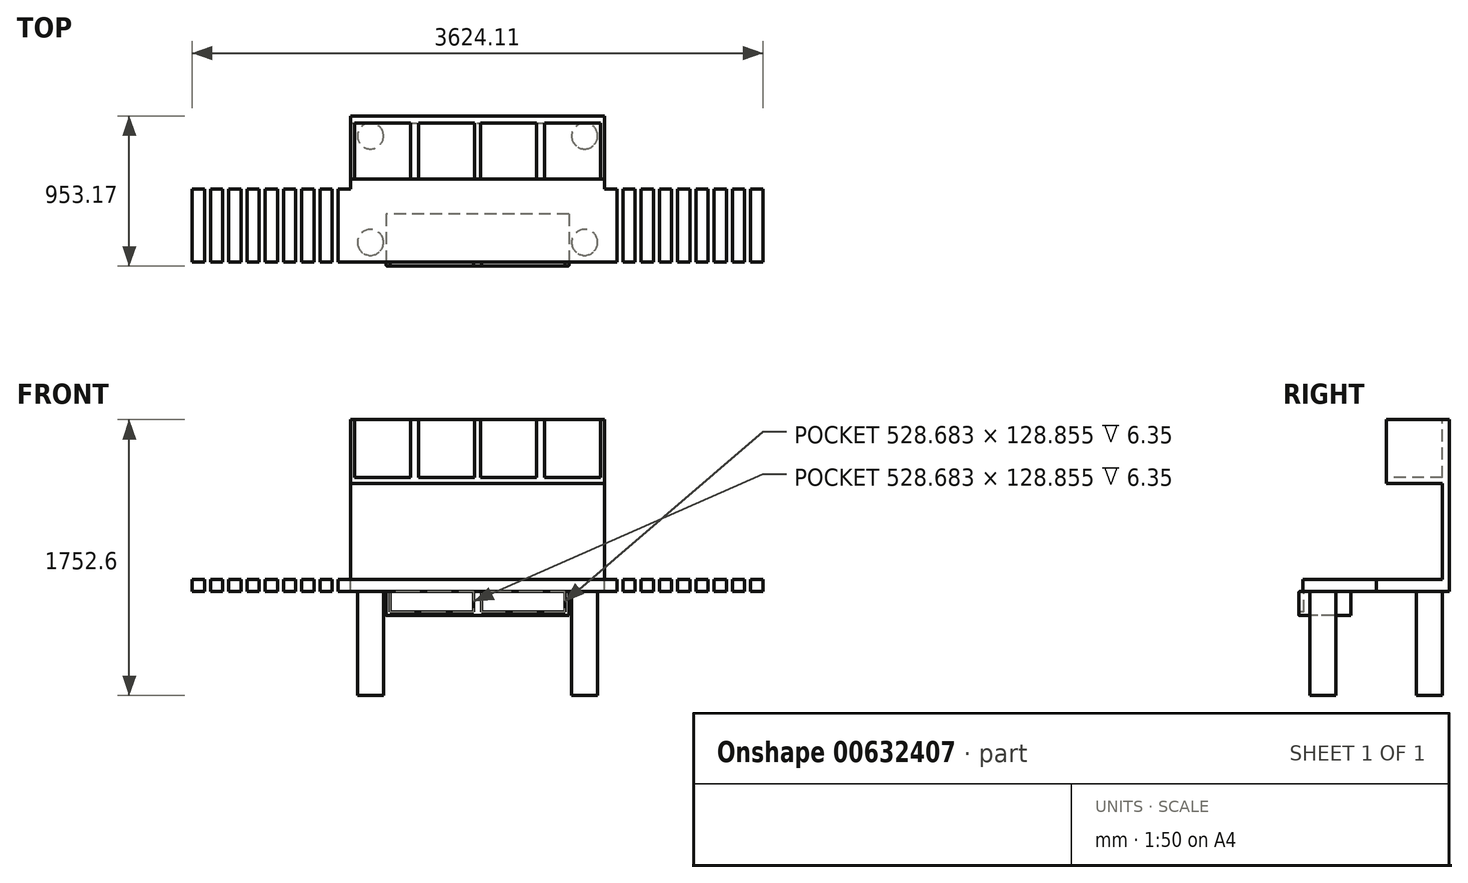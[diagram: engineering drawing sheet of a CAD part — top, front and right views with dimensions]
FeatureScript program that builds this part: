
annotation { "Feature Type Name" : "Feature", "Feature Type Description" : "" }
export const myFeature = defineFeature(function(context is Context, id is Id, definition is map)
    precondition{}
    {
        {
            var Q0;
            Q0=qCreatedBy(makeId("Top.planeOp"),FACE);
            var sketch = newSketch(context, id + "F0", { "sketchPlane" : qUnion([Q0])});
            skLineSegment(sketch, "E0.bottom", {"start": v(0, 0) * mm, "end": v(1613.94, 0) * mm});
            skLineSegment(sketch, "E0.top", {"start": v(0, 927.77) * mm, "end": v(1613.94, 927.77) * mm});
            skLineSegment(sketch, "E0.left", {"start": v(0, 0) * mm, "end": v(0, 927.77) * mm});
            skLineSegment(sketch, "E0.right", {"start": v(1613.94, 0) * mm, "end": v(1613.94, 927.77) * mm});
            skPoint(sketch, "E1", {"position": v(806.97, 0) * mm});
            skPoint(sketch, "E2", {"position": v(1613.94, 463.89) * mm});
            skLineSegment(sketch, "E3.bottom", {"start": v(1613.94, 463.89) * mm, "end": v(1691.25, 463.89) * mm});
            skLineSegment(sketch, "E3.top", {"start": v(1613.94, 0) * mm, "end": v(1691.25, 0) * mm});
            skLineSegment(sketch, "E3.left", {"start": v(1613.94, 463.89) * mm, "end": v(1613.94, 0) * mm});
            skLineSegment(sketch, "E3.right", {"start": v(1691.25, 463.89) * mm, "end": v(1691.25, 0) * mm});
            skPoint(sketch, "E4", {"position": v(1729.9, 463.89) * mm});
            skPoint(sketch, "E5", {"position": v(1729.9, 0) * mm});
            skLineSegment(sketch, "E6.bottom", {"start": v(1729.9, 463.89) * mm, "end": v(1807.22, 463.89) * mm});
            skLineSegment(sketch, "E6.top", {"start": v(1729.9, 0) * mm, "end": v(1807.22, 0) * mm});
            skLineSegment(sketch, "E6.left", {"start": v(1729.9, 463.89) * mm, "end": v(1729.9, 0) * mm});
            skLineSegment(sketch, "E6.right", {"start": v(1807.22, 463.89) * mm, "end": v(1807.22, 0) * mm});
            skPoint(sketch, "E7", {"position": v(1845.88, 463.89) * mm});
            skPoint(sketch, "E8", {"position": v(1845.88, 0) * mm});
            skLineSegment(sketch, "E9.bottom", {"start": v(1845.88, 463.89) * mm, "end": v(1923.2, 463.89) * mm});
            skLineSegment(sketch, "E9.top", {"start": v(1845.88, 0) * mm, "end": v(1923.2, 0) * mm});
            skLineSegment(sketch, "E9.left", {"start": v(1845.88, 463.89) * mm, "end": v(1845.88, 0) * mm});
            skLineSegment(sketch, "E9.right", {"start": v(1923.2, 463.89) * mm, "end": v(1923.2, 0) * mm});
            skPoint(sketch, "E10", {"position": v(1961.85, 463.89) * mm});
            skPoint(sketch, "E11", {"position": v(1961.85, 0) * mm});
            skLineSegment(sketch, "E12.bottom", {"start": v(1961.85, 463.89) * mm, "end": v(2039.17, 463.89) * mm});
            skLineSegment(sketch, "E12.top", {"start": v(1961.85, 0) * mm, "end": v(2039.17, 0) * mm});
            skLineSegment(sketch, "E12.left", {"start": v(1961.85, 463.89) * mm, "end": v(1961.85, 0) * mm});
            skLineSegment(sketch, "E12.right", {"start": v(2039.17, 463.89) * mm, "end": v(2039.17, 0) * mm});
            skPoint(sketch, "E13", {"position": v(2077.82, 463.89) * mm});
            skPoint(sketch, "E14", {"position": v(2077.82, 0) * mm});
            skLineSegment(sketch, "E15.bottom", {"start": v(2077.82, 463.89) * mm, "end": v(2155.14, 463.89) * mm});
            skLineSegment(sketch, "E15.top", {"start": v(2077.82, 0) * mm, "end": v(2155.14, 0) * mm});
            skLineSegment(sketch, "E15.left", {"start": v(2077.82, 463.89) * mm, "end": v(2077.82, 0) * mm});
            skLineSegment(sketch, "E15.right", {"start": v(2155.14, 463.89) * mm, "end": v(2155.14, 0) * mm});
            skPoint(sketch, "E16", {"position": v(2193.8, 463.89) * mm});
            skPoint(sketch, "E17", {"position": v(2193.8, 0) * mm});
            skLineSegment(sketch, "E18.bottom", {"start": v(2193.8, 463.89) * mm, "end": v(2271.1, 463.89) * mm});
            skLineSegment(sketch, "E18.top", {"start": v(2193.8, 0) * mm, "end": v(2271.1, 0) * mm});
            skLineSegment(sketch, "E18.left", {"start": v(2193.8, 463.89) * mm, "end": v(2193.8, 0) * mm});
            skLineSegment(sketch, "E18.right", {"start": v(2271.1, 463.89) * mm, "end": v(2271.1, 0) * mm});
            skPoint(sketch, "E19", {"position": v(2309.77, 463.89) * mm});
            skPoint(sketch, "E20", {"position": v(2309.77, 0) * mm});
            skLineSegment(sketch, "E21.bottom", {"start": v(2309.77, 463.89) * mm, "end": v(2387.08, 463.89) * mm});
            skLineSegment(sketch, "E21.top", {"start": v(2309.77, 0) * mm, "end": v(2387.08, 0) * mm});
            skLineSegment(sketch, "E21.left", {"start": v(2309.77, 463.89) * mm, "end": v(2309.77, 0) * mm});
            skLineSegment(sketch, "E21.right", {"start": v(2387.08, 463.89) * mm, "end": v(2387.08, 0) * mm});
            skPoint(sketch, "E22", {"position": v(2425.74, 463.89) * mm});
            skPoint(sketch, "E23", {"position": v(2425.74, 0) * mm});
            skLineSegment(sketch, "E24.bottom", {"start": v(2425.74, 463.89) * mm, "end": v(2503.05, 463.89) * mm});
            skLineSegment(sketch, "E24.top", {"start": v(2425.74, 0) * mm, "end": v(2503.05, 0) * mm});
            skLineSegment(sketch, "E24.left", {"start": v(2425.74, 463.89) * mm, "end": v(2425.74, 0) * mm});
            skLineSegment(sketch, "E24.right", {"start": v(2503.05, 463.89) * mm, "end": v(2503.05, 0) * mm});
            skPoint(sketch, "E25", {"position": v(2541.7, 463.89) * mm});
            skPoint(sketch, "E26", {"position": v(2541.7, 0) * mm});
            skLineSegment(sketch, "E27.bottom", {"start": v(2541.7, 463.89) * mm, "end": v(2619.02, 463.89) * mm});
            skLineSegment(sketch, "E27.top", {"start": v(2541.7, 0) * mm, "end": v(2619.02, 0) * mm});
            skLineSegment(sketch, "E27.left", {"start": v(2541.7, 463.89) * mm, "end": v(2541.7, 0) * mm});
            skLineSegment(sketch, "E27.right", {"start": v(2619.02, 463.89) * mm, "end": v(2619.02, 0) * mm});
            skPoint(sketch, "E28", {"position": v(-1005.09, 463.89) * mm});
            skPoint(sketch, "E29", {"position": v(-1005.09, 0) * mm});
            skLineSegment(sketch, "E30.bottom", {"start": v(-1005.09, 463.89) * mm, "end": v(-927.77, 463.89) * mm});
            skLineSegment(sketch, "E30.top", {"start": v(-1005.09, 0) * mm, "end": v(-927.77, 0) * mm});
            skLineSegment(sketch, "E30.left", {"start": v(-1005.09, 463.89) * mm, "end": v(-1005.09, 0) * mm});
            skLineSegment(sketch, "E30.right", {"start": v(-927.77, 463.89) * mm, "end": v(-927.77, 0) * mm});
            skPoint(sketch, "E31", {"position": v(-889.11, 463.89) * mm});
            skPoint(sketch, "E32", {"position": v(-889.11, 0) * mm});
            skLineSegment(sketch, "E33.bottom", {"start": v(-889.11, 463.89) * mm, "end": v(-811.8, 463.89) * mm});
            skLineSegment(sketch, "E33.top", {"start": v(-889.11, 0) * mm, "end": v(-811.8, 0) * mm});
            skLineSegment(sketch, "E33.left", {"start": v(-889.11, 463.89) * mm, "end": v(-889.11, 0) * mm});
            skLineSegment(sketch, "E33.right", {"start": v(-811.8, 463.89) * mm, "end": v(-811.8, 0) * mm});
            skPoint(sketch, "E34", {"position": v(-773.14, 463.89) * mm});
            skPoint(sketch, "E35", {"position": v(-773.14, 0) * mm});
            skLineSegment(sketch, "E36.bottom", {"start": v(-773.14, 463.89) * mm, "end": v(-695.83, 463.89) * mm});
            skLineSegment(sketch, "E36.top", {"start": v(-773.14, 0) * mm, "end": v(-695.83, 0) * mm});
            skLineSegment(sketch, "E36.left", {"start": v(-773.14, 463.89) * mm, "end": v(-773.14, 0) * mm});
            skLineSegment(sketch, "E36.right", {"start": v(-695.83, 463.89) * mm, "end": v(-695.83, 0) * mm});
            skPoint(sketch, "E37", {"position": v(-657.17, 463.89) * mm});
            skPoint(sketch, "E38", {"position": v(-657.17, 0) * mm});
            skLineSegment(sketch, "E39.bottom", {"start": v(-657.17, 463.89) * mm, "end": v(-579.86, 463.89) * mm});
            skLineSegment(sketch, "E39.top", {"start": v(-657.17, 0) * mm, "end": v(-579.86, 0) * mm});
            skLineSegment(sketch, "E39.left", {"start": v(-657.17, 463.89) * mm, "end": v(-657.17, 0) * mm});
            skLineSegment(sketch, "E39.right", {"start": v(-579.86, 463.89) * mm, "end": v(-579.86, 0) * mm});
            skPoint(sketch, "E40", {"position": v(-541.2, 463.89) * mm});
            skPoint(sketch, "E41", {"position": v(-541.2, 0) * mm});
            skLineSegment(sketch, "E42.bottom", {"start": v(-541.2, 463.89) * mm, "end": v(-463.89, 463.89) * mm});
            skLineSegment(sketch, "E42.top", {"start": v(-541.2, 0) * mm, "end": v(-463.89, 0) * mm});
            skLineSegment(sketch, "E42.left", {"start": v(-541.2, 463.89) * mm, "end": v(-541.2, 0) * mm});
            skLineSegment(sketch, "E42.right", {"start": v(-463.89, 463.89) * mm, "end": v(-463.89, 0) * mm});
            skPoint(sketch, "E43", {"position": v(-425.23, 463.89) * mm});
            skPoint(sketch, "E44", {"position": v(-425.23, 0) * mm});
            skLineSegment(sketch, "E45.bottom", {"start": v(-425.23, 463.89) * mm, "end": v(-347.91, 463.89) * mm});
            skLineSegment(sketch, "E45.top", {"start": v(-425.23, 0) * mm, "end": v(-347.91, 0) * mm});
            skLineSegment(sketch, "E45.left", {"start": v(-425.23, 463.89) * mm, "end": v(-425.23, 0) * mm});
            skLineSegment(sketch, "E45.right", {"start": v(-347.91, 463.89) * mm, "end": v(-347.91, 0) * mm});
            skPoint(sketch, "E46", {"position": v(-309.26, 463.89) * mm});
            skPoint(sketch, "E47", {"position": v(-309.26, 0) * mm});
            skLineSegment(sketch, "E48.bottom", {"start": v(-309.26, 463.89) * mm, "end": v(-231.94, 463.89) * mm});
            skLineSegment(sketch, "E48.top", {"start": v(-309.26, 0) * mm, "end": v(-231.94, 0) * mm});
            skLineSegment(sketch, "E48.left", {"start": v(-309.26, 463.89) * mm, "end": v(-309.26, 0) * mm});
            skLineSegment(sketch, "E48.right", {"start": v(-231.94, 463.89) * mm, "end": v(-231.94, 0) * mm});
            skPoint(sketch, "E49", {"position": v(-193.29, 463.89) * mm});
            skPoint(sketch, "E50", {"position": v(-193.29, 0) * mm});
            skLineSegment(sketch, "E51.bottom", {"start": v(-193.29, 463.89) * mm, "end": v(-115.97, 463.89) * mm});
            skLineSegment(sketch, "E51.top", {"start": v(-193.29, 0) * mm, "end": v(-115.97, 0) * mm});
            skLineSegment(sketch, "E51.left", {"start": v(-193.29, 463.89) * mm, "end": v(-193.29, 0) * mm});
            skLineSegment(sketch, "E51.right", {"start": v(-115.97, 463.89) * mm, "end": v(-115.97, 0) * mm});
            skPoint(sketch, "E52", {"position": v(0, 463.89) * mm});
            skLineSegment(sketch, "E53.bottom", {"start": v(0, 463.89) * mm, "end": v(-77.31, 463.89) * mm});
            skLineSegment(sketch, "E53.top", {"start": v(0, 0) * mm, "end": v(-77.31, 0) * mm});
            skLineSegment(sketch, "E53.left", {"start": v(0, 463.89) * mm, "end": v(0, 0) * mm});
            skLineSegment(sketch, "E53.right", {"start": v(-77.31, 463.89) * mm, "end": v(-77.31, 0) * mm});
            skSolve(sketch);
        }
        {
            var Q0;
            Q0 = qSketchRegion(id + "F0", true);
            extrude(context, id + "F1", {"entities" : qUnion([Q0]), "oppositeDirection" : true, "depth" : 76.2 * mm, "offsetDistance" : 25.4 * mm});
        }
        {
            var Q0;
            Q0=makeQuery(id+"F1.opExtrude","CAP_FACE",FACE,{"disambiguationData":[OSD([sQuery(id+"F0.wireOp",EDGE,"E0.bottom"),sQuery(id+"F0.wireOp",EDGE,"E0.top"),sQuery(id+"F0.wireOp",EDGE,"E0.left"),sQuery(id+"F0.wireOp",EDGE,"E0.right"),sQuery(id+"F0.wireOp",EDGE,"E3.bottom"),sQuery(id+"F0.wireOp",EDGE,"E3.top"),sQuery(id+"F0.wireOp",EDGE,"E3.right"),sQuery(id+"F0.wireOp",EDGE,"E53.bottom"),sQuery(id+"F0.wireOp",EDGE,"E53.top"),sQuery(id+"F0.wireOp",EDGE,"E53.right")])],"isStart":true});
            var sketch = newSketch(context, id + "F2", { "sketchPlane" : qUnion([Q0])});
            skPoint(sketch, "E54", {"position": v(0, 527.39) * mm});
            skPoint(sketch, "E55", {"position": v(1613.94, 527.39) * mm});
            skLineSegment(sketch, "E56.bottom", {"start": v(0, 527.39) * mm, "end": v(1613.94, 527.39) * mm});
            skLineSegment(sketch, "E56.top", {"start": v(0, 927.77) * mm, "end": v(1613.94, 927.77) * mm});
            skLineSegment(sketch, "E56.left", {"start": v(0, 527.39) * mm, "end": v(0, 927.77) * mm});
            skLineSegment(sketch, "E56.right", {"start": v(1613.94, 527.39) * mm, "end": v(1613.94, 927.77) * mm});
            skSolve(sketch);
        }
        {
            var Q0;
            Q0 = qSketchRegion(id + "F2", true);
            extrude(context, id + "F3", {"entities" : qUnion([Q0]), "operationType" : NewBodyOperationType.ADD, "depth" : 1016 * mm, "offsetDistance" : 25.4 * mm});
        }
        {
            var Q0;
            Q0=makeQuery(id+"F1.opExtrude","CAP_FACE",FACE,{"disambiguationData":[OSD([sQuery(id+"F0.wireOp",EDGE,"E0.bottom"),sQuery(id+"F0.wireOp",EDGE,"E0.top"),sQuery(id+"F0.wireOp",EDGE,"E0.left"),sQuery(id+"F0.wireOp",EDGE,"E0.right"),sQuery(id+"F0.wireOp",EDGE,"E3.bottom"),sQuery(id+"F0.wireOp",EDGE,"E3.top"),sQuery(id+"F0.wireOp",EDGE,"E3.right"),sQuery(id+"F0.wireOp",EDGE,"E53.bottom"),sQuery(id+"F0.wireOp",EDGE,"E53.top"),sQuery(id+"F0.wireOp",EDGE,"E53.right")])],"isStart":false});
            var sketch = newSketch(context, id + "F4", { "sketchPlane" : qUnion([Q0])});
            skCircle(sketch, "E57", {"center": v(127, -800.77) * mm, "radius": 82.55 * mm});
            skCircle(sketch, "E58", {"center": v(1486.94, -800.77) * mm, "radius": 82.55 * mm});
            skCircle(sketch, "E59", {"center": v(127, -125.13) * mm, "radius": 82.55 * mm});
            skCircle(sketch, "E60", {"center": v(1486.94, -125.13) * mm, "radius": 82.55 * mm});
            skSolve(sketch);
        }
        {
            var Q0;
            Q0 = qSketchRegion(id + "F4", true);
            extrude(context, id + "F5", {"entities" : qUnion([Q0]), "operationType" : NewBodyOperationType.ADD, "depth" : 660.4 * mm, "offsetDistance" : 25.4 * mm});
        }
        {
            var Q0;
            Q0=makeQuery(id+"F3.opExtrude","SWEPT_FACE",FACE,{"disambiguationData":[OSD([sQuery(id+"F2.wireOp",EDGE,"E56.bottom")])]});
            var sketch = newSketch(context, id + "F6", { "sketchPlane" : qUnion([Q0])});
            skLineSegment(sketch, "E61.bottom", {"start": v(0, 0) * mm, "end": v(1613.94, 0) * mm});
            skLineSegment(sketch, "E61.top", {"start": v(0, 609.6) * mm, "end": v(1613.94, 609.6) * mm});
            skLineSegment(sketch, "E61.left", {"start": v(0, 0) * mm, "end": v(0, 609.6) * mm});
            skLineSegment(sketch, "E61.right", {"start": v(1613.94, 0) * mm, "end": v(1613.94, 609.6) * mm});
            skSolve(sketch);
        }
        {
            var Q0;
            Q0 = qSketchRegion(id + "F6", true);
            extrude(context, id + "F7", {"entities" : qUnion([Q0]), "operationType" : NewBodyOperationType.REMOVE, "oppositeDirection" : true, "depth" : 355.6 * mm, "offsetDistance" : 25.4 * mm});
        }
        {
            var Q0;
            Q0=makeQuery(id+"F3.opExtrude","SWEPT_FACE",FACE,{"disambiguationData":[OSD([sQuery(id+"F2.wireOp",EDGE,"E56.bottom")])]});
            var sketch = newSketch(context, id + "F8", { "sketchPlane" : qUnion([Q0])});
            skPoint(sketch, "E62", {"position": v(25.4, 1016) * mm});
            skPoint(sketch, "E63", {"position": v(381, 1016) * mm});
            skPoint(sketch, "E64", {"position": v(431.8, 1016) * mm});
            skPoint(sketch, "E65", {"position": v(787.4, 1016) * mm});
            skPoint(sketch, "E66", {"position": v(826.54, 1016) * mm});
            skPoint(sketch, "E67", {"position": v(1182.14, 1016) * mm});
            skPoint(sketch, "E68", {"position": v(1232.94, 1016) * mm});
            skPoint(sketch, "E69", {"position": v(1588.54, 1016) * mm});
            skPoint(sketch, "E70", {"position": v(25.4, 647.7) * mm});
            skPoint(sketch, "E71", {"position": v(1588.54, 647.7) * mm});
            skLineSegment(sketch, "E72.bottom", {"start": v(25.4, 647.7) * mm, "end": v(381, 647.7) * mm});
            skLineSegment(sketch, "E72.top", {"start": v(25.4, 1016) * mm, "end": v(381, 1016) * mm});
            skLineSegment(sketch, "E72.left", {"start": v(25.4, 647.7) * mm, "end": v(25.4, 1016) * mm});
            skLineSegment(sketch, "E72.right", {"start": v(381, 647.7) * mm, "end": v(381, 1016) * mm});
            skLineSegment(sketch, "E73.bottom", {"start": v(431.8, 647.7) * mm, "end": v(787.4, 647.7) * mm});
            skLineSegment(sketch, "E73.top", {"start": v(431.8, 1016) * mm, "end": v(787.4, 1016) * mm});
            skLineSegment(sketch, "E73.left", {"start": v(431.8, 647.7) * mm, "end": v(431.8, 1016) * mm});
            skLineSegment(sketch, "E73.right", {"start": v(787.4, 647.7) * mm, "end": v(787.4, 1016) * mm});
            skLineSegment(sketch, "E74.bottom", {"start": v(826.54, 647.7) * mm, "end": v(1182.14, 647.7) * mm});
            skLineSegment(sketch, "E74.top", {"start": v(826.54, 1016) * mm, "end": v(1182.14, 1016) * mm});
            skLineSegment(sketch, "E74.left", {"start": v(826.54, 647.7) * mm, "end": v(826.54, 1016) * mm});
            skLineSegment(sketch, "E74.right", {"start": v(1182.14, 647.7) * mm, "end": v(1182.14, 1016) * mm});
            skLineSegment(sketch, "E75.bottom", {"start": v(1232.94, 647.7) * mm, "end": v(1588.54, 647.7) * mm});
            skLineSegment(sketch, "E75.top", {"start": v(1232.94, 1016) * mm, "end": v(1588.54, 1016) * mm});
            skLineSegment(sketch, "E75.left", {"start": v(1232.94, 647.7) * mm, "end": v(1232.94, 1016) * mm});
            skLineSegment(sketch, "E75.right", {"start": v(1588.54, 647.7) * mm, "end": v(1588.54, 1016) * mm});
            skSolve(sketch);
        }
        {
            var Q0;
            Q0 = qSketchRegion(id + "F8", true);
            extrude(context, id + "F9", {"entities" : qUnion([Q0]), "operationType" : NewBodyOperationType.REMOVE, "oppositeDirection" : true, "depth" : 355.6 * mm, "offsetDistance" : 25.4 * mm});
        }
        {
            var Q0;
            Q0=makeQuery(id+"F1.opExtrude","SWEPT_FACE",FACE,{"disambiguationData":[OSD([sQuery(id+"F0.wireOp",EDGE,"E0.bottom"),sQuery(id+"F0.wireOp",EDGE,"E3.top"),sQuery(id+"F0.wireOp",EDGE,"E53.top")])]});
            var sketch = newSketch(context, id + "F10", { "sketchPlane" : qUnion([Q0])});
            skPoint(sketch, "E76", {"position": v(227.49, -76.2) * mm});
            skPoint(sketch, "E77", {"position": v(1386.45, -76.2) * mm});
            skLineSegment(sketch, "E78.bottom", {"start": v(227.49, -76.2) * mm, "end": v(1386.45, -76.2) * mm});
            skLineSegment(sketch, "E78.top", {"start": v(227.49, -228.6) * mm, "end": v(1386.45, -228.6) * mm});
            skLineSegment(sketch, "E78.left", {"start": v(227.49, -76.2) * mm, "end": v(227.49, -228.6) * mm});
            skLineSegment(sketch, "E78.right", {"start": v(1386.45, -76.2) * mm, "end": v(1386.45, -228.6) * mm});
            skSolve(sketch);
        }
        {
            var Q0;
            Q0 = qSketchRegion(id + "F10", true);
            extrude(context, id + "F11", {"entities" : qUnion([Q0]), "operationType" : NewBodyOperationType.ADD, "oppositeDirection" : true, "depth" : 304.8 * mm, "offsetDistance" : 25.4 * mm, "hasSecondDirection" : true, "secondDirectionOppositeDirection" : false, "secondDirectionDepth" : 25.4 * mm});
        }
        {
            var Q0;
            Q0=makeQuery(id+"F11.opExtrude","CAP_FACE",FACE,{"disambiguationData":[OSD([sQuery(id+"F10.wireOp",EDGE,"E78.bottom"),sQuery(id+"F10.wireOp",EDGE,"E78.top"),sQuery(id+"F10.wireOp",EDGE,"E78.left"),sQuery(id+"F10.wireOp",EDGE,"E78.right")])],"isStart":true});
            var sketch = newSketch(context, id + "F12", { "sketchPlane" : qUnion([Q0])});
            skPoint(sketch, "E79", {"position": v(1386.45, -228.6) * mm});
            skPoint(sketch, "E80", {"position": v(252.89, -76.2) * mm});
            skPoint(sketch, "E81", {"position": v(806.97, -76.2) * mm});
            skPoint(sketch, "E82", {"position": v(781.57, -76.2) * mm});
            skPoint(sketch, "E83", {"position": v(832.37, -76.2) * mm});
            skPoint(sketch, "E84", {"position": v(1361.05, -76.2) * mm});
            skPoint(sketch, "E85", {"position": v(252.89, -205.06) * mm});
            skPoint(sketch, "E86", {"position": v(781.57, -205.06) * mm});
            skPoint(sketch, "E87", {"position": v(832.37, -205.06) * mm});
            skPoint(sketch, "E88", {"position": v(1361.05, -205.06) * mm});
            skLineSegment(sketch, "E89.bottom", {"start": v(252.89, -205.06) * mm, "end": v(781.57, -205.06) * mm});
            skLineSegment(sketch, "E89.top", {"start": v(252.89, -76.2) * mm, "end": v(781.57, -76.2) * mm});
            skLineSegment(sketch, "E89.left", {"start": v(252.89, -205.06) * mm, "end": v(252.89, -76.2) * mm});
            skLineSegment(sketch, "E89.right", {"start": v(781.57, -205.06) * mm, "end": v(781.57, -76.2) * mm});
            skLineSegment(sketch, "E90.bottom", {"start": v(832.37, -205.06) * mm, "end": v(1361.05, -205.06) * mm});
            skLineSegment(sketch, "E90.top", {"start": v(832.37, -76.2) * mm, "end": v(1361.05, -76.2) * mm});
            skLineSegment(sketch, "E90.left", {"start": v(832.37, -205.06) * mm, "end": v(832.37, -76.2) * mm});
            skLineSegment(sketch, "E90.right", {"start": v(1361.05, -205.06) * mm, "end": v(1361.05, -76.2) * mm});
            skSolve(sketch);
        }
        {
            var Q0;
            Q0 = qSketchRegion(id + "F12", true);
            extrude(context, id + "F13", {"entities" : qUnion([Q0]), "operationType" : NewBodyOperationType.REMOVE, "oppositeDirection" : true, "depth" : 31.75 * mm, "offsetDistance" : 25.4 * mm});
        }
        {
            var Q0;
            {var subQ0=sQuery(id+"F10.wireOp",EDGE,"E78.bottom");var subQ1=sQuery(id+"F10.wireOp",EDGE,"E78.left");Q0=makeQuery(id+"F13.boolean.opBoolean","SPLIT",EDGE,{"disambiguationData":[TD([makeQuery(id+"F11.opExtrude","SWEPT_FACE",FACE,{"disambiguationData":[OSD([subQ1])]})])],"derivedFrom":makeQuery(id+"F11.opExtrude","CAP_EDGE",EDGE,{"disambiguationData":[OSD([subQ0])],"isStart":true})});}
            var Q1;
            {var subQ0=sQuery(id+"F10.wireOp",EDGE,"E78.bottom");var subQ1=sQuery(id+"F10.wireOp",EDGE,"E78.left");Q1=makeQuery(id+"F11.boolean.opBoolean","SPLIT",EDGE,{"disambiguationData":[topologyDisambiguationEdgeConnected([makeQuery(id+"F11.opExtrude","SWEPT_FACE",FACE,{"disambiguationData":[OSD([subQ0])]})])],"derivedFrom":makeQuery(id+"F11.opExtrude","SWEPT_EDGE",EDGE,{"disambiguationData":[OSD([sQuery(id+"F0.wireOp",EDGE,"E0.bottom"),sQuery(id+"F0.wireOp",EDGE,"E3.top"),sQuery(id+"F0.wireOp",EDGE,"E53.top"),subQ0,subQ1])]})});}
            var Q2;
            Q2=makeQuery(id+"F11.opExtrude","CAP_EDGE",EDGE,{"disambiguationData":[OSD([sQuery(id+"F10.wireOp",EDGE,"E78.left")])],"isStart":true});
            fillet(context, id + "F14", {"entities" : qUnion([Q0, Q1, Q2]), "radius" : 5.08 * mm, "tangentPropagation" : true, "allowEdgeOverflow" : false});
        }
        {
            var Q0;
            {var subQ0=sQuery(id+"F10.wireOp",EDGE,"E78.bottom");Q0=makeQuery(id+"F13.boolean.opBoolean","SPLIT",EDGE,{"disambiguationData":[TD([makeQuery(id+"F13.opExtrude","SWEPT_FACE",FACE,{"disambiguationData":[OSD([sQuery(id+"F12.wireOp",EDGE,"E89.right")])]})])],"derivedFrom":makeQuery(id+"F11.opExtrude","CAP_EDGE",EDGE,{"disambiguationData":[OSD([subQ0])],"isStart":true})});}
            var Q1;
            {var subQ0=sQuery(id+"F10.wireOp",EDGE,"E78.bottom");var subQ1=sQuery(id+"F12.wireOp",EDGE,"E90.left");Q1=makeQuery(id+"F13.boolean.opBoolean","COPY",EDGE,{"disambiguationData":[topologyDisambiguationEdgeConnected([makeQuery(id+"F11.opExtrude","SWEPT_FACE",FACE,{"disambiguationData":[OSD([subQ0])]})])],"derivedFrom":makeQuery(id+"F13.opExtrude","SWEPT_EDGE",EDGE,{"disambiguationData":[OSD([subQ0,sQuery(id+"F12.wireOp",EDGE,"E90.top"),subQ1])]})});}
            var Q2;
            {var subQ0=sQuery(id+"F10.wireOp",EDGE,"E78.bottom");var subQ1=sQuery(id+"F12.wireOp",EDGE,"E89.right");Q2=makeQuery(id+"F13.boolean.opBoolean","COPY",EDGE,{"disambiguationData":[topologyDisambiguationEdgeConnected([makeQuery(id+"F11.opExtrude","SWEPT_FACE",FACE,{"disambiguationData":[OSD([subQ0])]})])],"derivedFrom":makeQuery(id+"F13.opExtrude","SWEPT_EDGE",EDGE,{"disambiguationData":[OSD([subQ0,sQuery(id+"F12.wireOp",EDGE,"E89.top"),subQ1])]})});}
            var Q3;
            Q3=makeQuery(id+"F13.boolean.opBoolean","COPY",EDGE,{"derivedFrom":makeQuery(id+"F13.opExtrude","CAP_EDGE",EDGE,{"disambiguationData":[OSD([sQuery(id+"F12.wireOp",EDGE,"E89.right")])],"isStart":true})});
            var Q4;
            Q4=makeQuery(id+"F13.boolean.opBoolean","COPY",EDGE,{"derivedFrom":makeQuery(id+"F13.opExtrude","CAP_EDGE",EDGE,{"disambiguationData":[OSD([sQuery(id+"F12.wireOp",EDGE,"E90.left")])],"isStart":true})});
            fillet(context, id + "F15", {"entities" : qUnion([Q0, Q1, Q2, Q3, Q4]), "radius" : 5.08 * mm, "tangentPropagation" : true, "allowEdgeOverflow" : false});
        }
        {
            var Q0;
            {var subQ0=sQuery(id+"F10.wireOp",EDGE,"E78.bottom");var subQ1=sQuery(id+"F10.wireOp",EDGE,"E78.right");Q0=makeQuery(id+"F13.boolean.opBoolean","SPLIT",EDGE,{"disambiguationData":[TD([makeQuery(id+"F11.opExtrude","SWEPT_FACE",FACE,{"disambiguationData":[OSD([subQ1])]})])],"derivedFrom":makeQuery(id+"F11.opExtrude","CAP_EDGE",EDGE,{"disambiguationData":[OSD([subQ0])],"isStart":true})});}
            var Q1;
            {var subQ0=sQuery(id+"F10.wireOp",EDGE,"E78.bottom");var subQ1=sQuery(id+"F10.wireOp",EDGE,"E78.right");Q1=makeQuery(id+"F11.boolean.opBoolean","SPLIT",EDGE,{"disambiguationData":[topologyDisambiguationEdgeConnected([makeQuery(id+"F11.opExtrude","SWEPT_FACE",FACE,{"disambiguationData":[OSD([subQ0])]})])],"derivedFrom":makeQuery(id+"F11.opExtrude","SWEPT_EDGE",EDGE,{"disambiguationData":[OSD([sQuery(id+"F0.wireOp",EDGE,"E0.bottom"),sQuery(id+"F0.wireOp",EDGE,"E3.top"),sQuery(id+"F0.wireOp",EDGE,"E53.top"),subQ0,subQ1])]})});}
            var Q2;
            Q2=makeQuery(id+"F11.opExtrude","CAP_EDGE",EDGE,{"disambiguationData":[OSD([sQuery(id+"F10.wireOp",EDGE,"E78.right")])],"isStart":true});
            fillet(context, id + "F16", {"entities" : qUnion([Q0, Q1, Q2]), "radius" : 5.08 * mm, "tangentPropagation" : true, "allowEdgeOverflow" : false});
        }
    });
